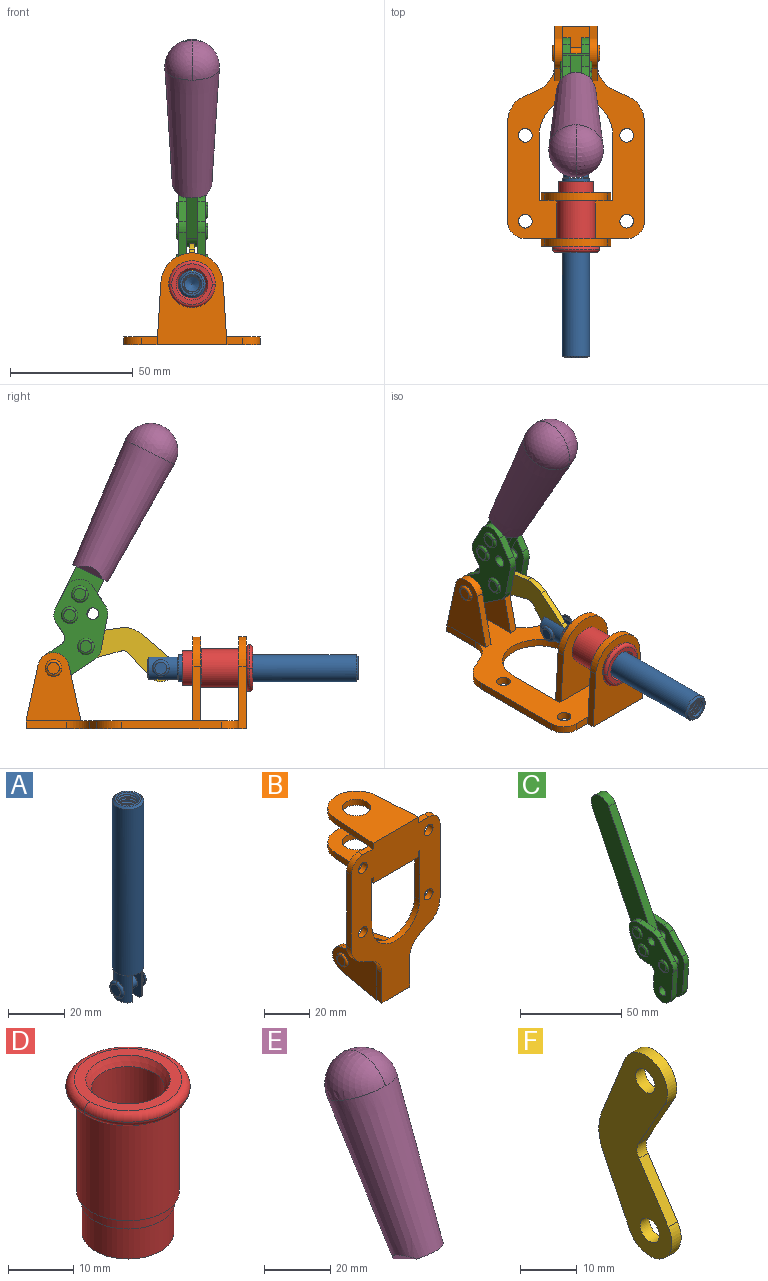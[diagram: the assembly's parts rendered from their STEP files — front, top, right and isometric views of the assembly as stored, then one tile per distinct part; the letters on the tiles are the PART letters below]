
ASSEMBLY  parts=6 mates=6
PART A: 48 faces, bbox 12.6x11.1x86.1 mm
  f0: torus R=2.41mm, axis (-1,0,0), area 15mm2, adj f30,f32,f34
  f1: torus R=2.41mm, axis (-1,0,0), area 15mm2, adj f29,f31,f33
  f2: cylinder r=5.54mm len=72.39mm, axis (0,0,1), area 2518.5mm2, adj f3,f4,f42,f43
  f3: cone r=5.54mm half-angle=45deg, axis (0,0,1), area 7.6mm2, adj f2,f5,f41
  f4: cone r=5.54mm half-angle=45deg, axis (0,0,-1), area 34.9mm2, adj f2,f39
  f5: cylinder r=5.08mm len=11.48mm, axis (0,0,1), area 108.3mm2, adj f3,f7,f8,f41
  f6: cylinder r=2.41mm len=4.83mm, axis (-1,0,0), area 71.2mm2, adj f40,f41
  f7: cylinder r=2.41mm len=4.83mm, axis (-1,0,0), area 7.6mm2, adj f5,f34
  f8: cone r=5.08mm half-angle=45deg, axis (0,0,1), area 10.6mm2, adj f5,f37,f41
  f9: cone r=3.98mm half-angle=45deg, axis (0,0,1), area 17.6mm2, adj f27,f39,f45,f46,f47
  f10: cylinder r=2.41mm len=4.83mm, axis (-1,0,0), area 7.6mm2, adj f33,f38
  f11: cylinder r=3.2mm len=6.4mm, axis (0,0,1), area 78.4mm2, adj f12,f28,f44,f45,f47
  f12: cylinder r=3.2mm len=6.4mm, axis (0,0,1), area 10.5mm2, adj f11,f13,f45,f47
  f13: cylinder r=3.2mm len=6.4mm, axis (0,0,1), area 10.5mm2, adj f12,f14,f45,f47
  f14: cylinder r=3.2mm len=6.4mm, axis (0,0,1), area 10.5mm2, adj f13,f15,f45,f47
  f15: cylinder r=3.2mm len=6.4mm, axis (0,0,1), area 10.5mm2, adj f14,f16,f45,f47
  f16: cylinder r=3.2mm len=6.4mm, axis (0,0,1), area 10.5mm2, adj f15,f17,f45,f47
  f17: cylinder r=3.2mm len=6.4mm, axis (0,0,1), area 10.5mm2, adj f16,f18,f45,f47
  f18: cylinder r=3.2mm len=6.4mm, axis (0,0,1), area 10.5mm2, adj f17,f19,f45,f47
  f19: cylinder r=3.2mm len=6.4mm, axis (0,0,1), area 10.5mm2, adj f18,f20,f45,f47
  f20: cylinder r=3.2mm len=6.4mm, axis (0,0,1), area 10.5mm2, adj f19,f21,f45,f47
  f21: cylinder r=3.2mm len=6.4mm, axis (0,0,1), area 10.5mm2, adj f20,f22,f45,f47
  f22: cylinder r=3.2mm len=6.4mm, axis (0,0,1), area 10.5mm2, adj f21,f23,f45,f47
  f23: cylinder r=3.2mm len=6.4mm, axis (0,0,1), area 10.5mm2, adj f22,f24,f45,f47
  f24: cylinder r=3.2mm len=6.4mm, axis (0,0,1), area 10.5mm2, adj f23,f25,f45,f47
  f25: cylinder r=3.2mm len=6.4mm, axis (0,0,1), area 10.5mm2, adj f24,f26,f45,f47
  f26: cylinder r=3.2mm len=6.4mm, axis (0,0,1), area 10.5mm2, adj f25,f27,f45,f47
  f27: cylinder r=3.2mm len=6.4mm, axis (0,0,1), area 7.4mm2, adj f9,f26,f45,f47
  f28: cone r=3.2mm half-angle=60deg, axis (0,0,1), area 37.2mm2, adj f11
  f29: plane 4.83x4.83mm, normal (-1,0,0), area 18.3mm2, adj f1,f31
  f30: plane 4.83x4.83mm, normal (1,0,0), area 18.3mm2, adj f0,f32
  f31: torus R=2.41mm, axis (-1,0,0), area 15mm2, adj f1,f29,f33
  f32: torus R=2.41mm, axis (-1,0,0), area 15mm2, adj f0,f30,f34
  f33: plane 6.83x6.83mm, normal (1,0,0), area 18.3mm2, adj f1,f10,f31
  f34: plane 6.83x6.83mm, normal (-1,0,0), area 18.3mm2, adj f0,f7,f32
  f35: cone r=5.08mm half-angle=45deg, axis (0,0,1), area 10.6mm2, adj f36,f38,f40
  f36: plane 7.25x1.97mm, normal (0,0,-1), area 10mm2, adj f35,f40
  f37: plane 7.25x1.97mm, normal (0,0,-1), area 10mm2, adj f8,f41
  f38: cylinder r=5.08mm len=11.48mm, axis (0,0,1), area 108.3mm2, adj f10,f35,f40,f42
  f39: plane 9.55x9.55mm, normal (0,0,1), area 22mm2, adj f4,f9
  f40: plane 12.76x10.09mm, normal (1,0,0), area 95.7mm2, adj f6,f35,f36,f38,f42,f43
  f41: plane 12.76x10.09mm, normal (-1,0,0), area 95.7mm2, adj f3,f5,f6,f8,f37,f43
  f42: cone r=5.54mm half-angle=45deg, axis (0,0,1), area 7.6mm2, adj f2,f38,f40
  f43: plane 11.07x4.7mm, normal (0,0,-1), area 50.4mm2, adj f2,f40,f41
  f44: plane 0.89x0.62mm, normal (-1,0,0), area 0.3mm2, adj f11,f45,f46,f47
  f45: bspline ~24.8x7.63mm, area 266.6mm2, adj f9,f11,f12,f13,f14,f15,f16,f17
  f46: bspline ~24.87x7.63mm, area 73.6mm2, adj f9,f44,f45,f47
  f47: bspline ~24.98x7.63mm, area 272.5mm2, adj f9,f11,f12,f13,f14,f15,f16,f17
PART B: 55 faces, bbox 55.7x37.4x89.8 mm
  f0: torus R=2.41mm, axis (-1,0,0), area 15mm2, adj f11,f15,f25
  f1: torus R=2.41mm, axis (-1,0,0), area 15mm2, adj f10,f12,f22
  f2: cylinder r=2.78mm len=5.56mm, axis (0,-1,0), area 54.2mm2, adj f30,f54
  f3: cylinder r=14.99mm len=29.97mm, axis (0,-1,0), area 145.9mm2, adj f30,f49,f53,f54
  f4: cylinder r=2.78mm len=5.56mm, axis (0,-1,0), area 54.2mm2, adj f30,f54
  f5: cylinder r=2.78mm len=5.56mm, axis (0,-1,0), area 54.2mm2, adj f30,f54
  f6: cylinder r=2.78mm len=5.56mm, axis (0,-1,0), area 54.2mm2, adj f30,f54
  f7: cylinder r=6.35mm len=12.7mm, axis (0,0,1), area 123.6mm2, adj f27,f51
  f8: cylinder r=6.35mm len=12.7mm, axis (0,0,-1), area 124.7mm2, adj f21,f35
  f9: cylinder r=2.41mm len=11.18mm, axis (-1,0,0), area 169.4mm2, adj f16,f19
  f10: plane 4.83x4.83mm, normal (1,0,0), area 18.3mm2, adj f1,f12
  f11: plane 4.83x4.83mm, normal (-1,0,0), area 18.3mm2, adj f0,f15
  f12: torus R=2.41mm, axis (-1,0,0), area 15mm2, adj f1,f10,f22
  f13: cylinder r=6.35mm len=12.41mm, axis (1,0,0), area 53.4mm2, adj f18,f19,f22,f23
  f14: cylinder r=6.35mm len=12.41mm, axis (-1,0,0), area 53.4mm2, adj f16,f17,f24,f25
  f15: torus R=2.41mm, axis (-1,0,0), area 15mm2, adj f0,f11,f25
  f16: plane 27.86x22.35mm, normal (1,0,0), area 425.4mm2, adj f9,f14,f17,f24,f30
  f17: plane 22.86x4.97mm, normal (0,0.21,0.98), area 72.5mm2, adj f14,f16,f25,f30
  f18: plane 22.86x4.97mm, normal (0,0.21,0.98), area 72.5mm2, adj f13,f19,f22,f30
  f19: plane 27.86x22.35mm, normal (-1,0,0), area 425.4mm2, adj f9,f13,f18,f23,f30
  f20: cylinder r=12.7mm len=25.35mm, axis (0,0,-1), area 119.8mm2, adj f21,f34,f35,f36
  f21: plane 34.21x28.07mm, normal (0,0,-1), area 702.4mm2, adj f8,f20,f30,f34,f36
  f22: plane 27.96x22.45mm, normal (1,0,0), area 407.2mm2, adj f1,f12,f13,f18,f23,f30,f42,f43
  f23: plane 22.86x4.97mm, normal (0,0.21,-0.98), area 72.5mm2, adj f13,f19,f22,f44
  f24: plane 22.86x4.97mm, normal (0,0.21,-0.98), area 72.5mm2, adj f14,f16,f25,f44
  f25: plane 27.86x22.35mm, normal (-1,0,0), area 407.1mm2, adj f0,f14,f15,f17,f24,f30,f45,f46
  f26: plane 3.1x0.95mm, normal (0,0,-1), area 2.7mm2, adj f30,f49,f50,f54
  f27: plane 34.21x28.07mm, normal (0,0,1), area 702.4mm2, adj f7,f28,f30,f50,f52
  f28: cylinder r=12.7mm len=25.35mm, axis (0,0,1), area 118.8mm2, adj f27,f50,f51,f52
  f29: plane 3.1x0.95mm, normal (0,0,-1), area 2.7mm2, adj f30,f52,f53,f54
  f30: plane 86.54x55.63mm, normal (0,1,0), area 2362.9mm2, adj f2,f3,f4,f5,f6,f16,f17,f18
  f31: plane 40.56x3.1mm, normal (-1,0,0), area 125.7mm2, adj f30,f32,f48,f54
  f32: cylinder r=7.11mm len=7.11mm, axis (0,-1,0), area 34.6mm2, adj f30,f31,f33,f54
  f33: plane 6.67x3.1mm, normal (0,0,1), area 20.4mm2, adj f30,f32,f34,f54
  f34: plane 25.39x3.13mm, normal (-1,0.06,0), area 79.5mm2, adj f20,f21,f33,f35,f54
  f35: plane 37.31x28.45mm, normal (0,0,1), area 789.9mm2, adj f8,f20,f34,f36,f54
  f36: plane 25.39x3.13mm, normal (1,0.06,0), area 79.5mm2, adj f20,f21,f35,f37,f54
  f37: plane 6.67x3.1mm, normal (0,0,1), area 20.4mm2, adj f30,f36,f38,f54
  f38: cylinder r=7.11mm len=7.11mm, axis (0,-1,0), area 34.6mm2, adj f30,f37,f39,f54
  f39: plane 40.56x3.1mm, normal (1,0,0), area 125.7mm2, adj f30,f38,f40,f54
  f40: cylinder r=11.18mm len=10.16mm, axis (0,-1,0), area 39.5mm2, adj f30,f39,f41,f54
  f41: plane 6.09x3.1mm, normal (0.42,0,-0.91), area 20.8mm2, adj f30,f40,f42,f54
  f42: cylinder r=11.18mm len=9.41mm, axis (0,-1,0), area 37.2mm2, adj f22,f30,f41,f43,f54
  f43: plane 16.5x3.1mm, normal (1,0,0), area 51.1mm2, adj f22,f42,f44,f54
  f44: plane 17.37x3.1mm, normal (0,0,-1), area 53.8mm2, adj f23,f24,f30,f43,f45,f54
  f45: plane 16.5x3.1mm, normal (-1,0,0), area 51.1mm2, adj f25,f44,f46,f54
  f46: cylinder r=11.18mm len=9.41mm, axis (0,-1,0), area 37.2mm2, adj f25,f30,f45,f47,f54
  f47: plane 6.09x3.1mm, normal (-0.42,0,-0.91), area 20.8mm2, adj f30,f46,f48,f54
  f48: cylinder r=11.18mm len=10.16mm, axis (0,-1,0), area 39.5mm2, adj f30,f31,f47,f54
  f49: plane 26.54x3.1mm, normal (-1,0,0), area 82.3mm2, adj f3,f26,f30,f54
  f50: plane 25.39x3.1mm, normal (1,0.06,0), area 78.8mm2, adj f26,f27,f28,f51,f54
  f51: plane 37.31x28.45mm, normal (0,0,-1), area 789.9mm2, adj f7,f28,f50,f52,f54
  f52: plane 25.39x3.1mm, normal (-1,0.06,0), area 78.8mm2, adj f27,f28,f29,f51,f54
  f53: plane 26.54x3.1mm, normal (1,0,0), area 82.3mm2, adj f3,f29,f30,f54
  f54: plane 89.66x55.63mm, normal (0,-1,0), area 2678.5mm2, adj f2,f3,f4,f5,f6,f26,f29,f31
PART C: 59 faces, bbox 12.9x60.2x99.6 mm
  f0: torus R=2.39mm, axis (-1,0,0), area 14.9mm2, adj f20,f43,f51
  f1: torus R=2.39mm, axis (-1,0,0), area 14.9mm2, adj f19,f42,f51
  f2: torus R=2.39mm, axis (-1,0,0), area 14.9mm2, adj f18,f35,f51
  f3: torus R=2.39mm, axis (-1,0,0), area 14.9mm2, adj f14,f17,f23
  f4: torus R=2.39mm, axis (-1,0,0), area 14.9mm2, adj f13,f16,f23
  f5: torus R=2.39mm, axis (-1,0,0), area 14.9mm2, adj f12,f15,f23
  f6: cylinder r=2.39mm len=4.78mm, axis (1,0,0), area 46.5mm2, adj f48,f50,f51
  f7: cylinder r=2.39mm len=4.78mm, axis (1,0,0), area 46.5mm2, adj f50,f51
  f8: cylinder r=6.35mm len=12.68mm, axis (1,0,0), area 61.8mm2, adj f38,f39,f50,f51
  f9: cylinder r=2.39mm len=4.78mm, axis (-1,0,0), area 70.5mm2, adj f46,f50
  f10: cylinder r=2.39mm len=4.78mm, axis (-1,0,0), area 46.5mm2, adj f23,f45,f46
  f11: cylinder r=2.39mm len=4.78mm, axis (-1,0,0), area 46.5mm2, adj f23,f46
  f12: plane 4.78x4.78mm, normal (1,0,0), area 17.9mm2, adj f5,f15
  f13: plane 4.78x4.78mm, normal (1,0,0), area 17.9mm2, adj f4,f16
  f14: plane 4.78x4.78mm, normal (1,0,0), area 17.9mm2, adj f3,f17
  f15: torus R=2.39mm, axis (-1,0,0), area 14.9mm2, adj f5,f12,f23
  f16: torus R=2.39mm, axis (-1,0,0), area 14.9mm2, adj f4,f13,f23
  f17: torus R=2.39mm, axis (-1,0,0), area 14.9mm2, adj f3,f14,f23
  f18: plane 4.78x4.78mm, normal (-1,0,0), area 17.9mm2, adj f2,f35
  f19: plane 4.78x4.78mm, normal (-1,0,0), area 17.9mm2, adj f1,f42
  f20: plane 4.78x4.78mm, normal (-1,0,0), area 17.9mm2, adj f0,f43
  f21: plane 2.26x0.2mm, normal (1,0,0), area 0.2mm2, adj f31,f44
  f22: plane 2.26x0.2mm, normal (-1,0,0), area 0.2mm2, adj f41,f44
  f23: plane 39.37x30.77mm, normal (1,0,0), area 565.5mm2, adj f3,f4,f5,f10,f11,f15,f16,f17
  f24: cylinder r=6.1mm len=4.15mm, axis (-1,0,0), area 14.7mm2, adj f23,f25,f32,f46
  f25: plane 10.25x9.01mm, normal (0,-0.75,0.66), area 42.3mm2, adj f23,f24,f26,f46
  f26: cylinder r=6.35mm len=4.64mm, axis (-1,0,0), area 15.6mm2, adj f23,f25,f27,f46
  f27: plane 15.84x3.1mm, normal (0,-1,-0.07), area 49.2mm2, adj f23,f26,f28,f46
  f28: cylinder r=6.35mm len=12.68mm, axis (-1,0,0), area 61.8mm2, adj f23,f27,f29,f46
  f29: plane 8.11x3.1mm, normal (0,1,0.07), area 25.2mm2, adj f23,f28,f30,f46
  f30: cylinder r=3.05mm len=3.25mm, axis (-1,0,0), area 14.8mm2, adj f23,f29,f31,f46
  f31: plane 5.99x3.1mm, normal (0,0.07,-1), area 18.6mm2, adj f21,f23,f30,f44,f46
  f32: plane 9.5x3.1mm, normal (0,-0.07,1), area 29.5mm2, adj f23,f24,f33,f46,f47
  f33: cylinder r=6.1mm len=8.63mm, axis (-1,0,0), area 39.1mm2, adj f23,f32,f34,f47
  f34: plane 8.65x3.96mm, normal (0,0.91,-0.42), area 29.5mm2, adj f23,f33,f44,f47
  f35: torus R=2.39mm, axis (-1,0,0), area 14.9mm2, adj f2,f18,f51
  f36: plane 10.25x9.01mm, normal (0,-0.75,0.66), area 42.3mm2, adj f37,f49,f50,f51
  f37: cylinder r=6.35mm len=4.64mm, axis (1,0,0), area 15.6mm2, adj f36,f38,f50,f51
  f38: plane 15.84x3.1mm, normal (0,-1,-0.07), area 49.2mm2, adj f8,f37,f50,f51
  f39: plane 8.11x3.1mm, normal (0,1,0.07), area 25.2mm2, adj f8,f40,f50,f51
  f40: cylinder r=3.05mm len=3.25mm, axis (1,0,0), area 14.8mm2, adj f39,f41,f50,f51
  f41: plane 5.99x3.1mm, normal (0,0.07,-1), area 18.6mm2, adj f22,f40,f44,f50,f51
  f42: torus R=2.39mm, axis (-1,0,0), area 14.9mm2, adj f1,f19,f51
  f43: torus R=2.39mm, axis (-1,0,0), area 14.9mm2, adj f0,f20,f51
  f44: cylinder r=6.35mm len=12.12mm, axis (-1,0,0), area 128.9mm2, adj f21,f22,f23,f31,f34,f41,f46,f47
  f45: plane 2.65x1.35mm, normal (1,0,0), area 1mm2, adj f10,f55
  f46: plane 39.08x20.42mm, normal (-1,0,0), area 412.5mm2, adj f9,f10,f11,f24,f25,f26,f27,f28
  f47: plane 77.62x39.82mm, normal (1,0,0), area 850mm2, adj f32,f33,f34,f44,f53,f54,f55
  f48: plane 2.65x1.35mm, normal (-1,0,0), area 1mm2, adj f6,f55
  f49: cylinder r=6.1mm len=4.15mm, axis (1,0,0), area 14.7mm2, adj f36,f50,f51,f56
  f50: plane 39.08x20.42mm, normal (1,0,0), area 412.5mm2, adj f6,f7,f8,f9,f36,f37,f38,f39
  f51: plane 39.37x30.77mm, normal (-1,0,0), area 565.5mm2, adj f0,f1,f2,f6,f7,f8,f35,f36
  f52: plane 8.65x3.96mm, normal (0,0.91,-0.42), area 29.5mm2, adj f44,f51,f57,f58
  f53: plane 68.49x33.4mm, normal (0,0.9,-0.44), area 358.1mm2, adj f44,f47,f54,f58
  f54: cylinder r=6.35mm len=12.06mm, axis (1,0,0), area 93.7mm2, adj f47,f53,f55,f58
  f55: plane 68.49x33.4mm, normal (0,-0.9,0.44), area 358.1mm2, adj f44,f45,f46,f47,f48,f50,f54,f58
  f56: plane 9.5x3.1mm, normal (0,-0.07,1), area 29.5mm2, adj f49,f50,f51,f57,f58
  f57: cylinder r=6.1mm len=8.63mm, axis (1,0,0), area 39.1mm2, adj f51,f52,f56,f58
  f58: plane 77.62x39.82mm, normal (-1,0,0), area 850mm2, adj f44,f52,f53,f54,f55,f56,f57
PART D: 15 faces, bbox 20.6x20.6x28.7 mm
  f0: torus R=8.26mm, axis (0,0,1), area 56.8mm2, adj f1,f10,f12
  f1: torus R=8.26mm, axis (0,0,1), area 56.8mm2, adj f0,f6,f13
  f2: cylinder r=5.59mm len=25.91mm, axis (0,0,1), area 909.6mm2, adj f3,f4
  f3: cone r=6.86mm half-angle=45deg, axis (0,0,-1), area 70.2mm2, adj f2,f14
  f4: cone r=6.47mm half-angle=30deg, axis (0,0,1), area 66.7mm2, adj f2,f13
  f5: cylinder r=7.04mm len=14.07mm, axis (0,0,1), area 252.6mm2, adj f11,f14
  f6: torus R=8.26mm, axis (0,0,1), area 56.8mm2, adj f1,f12,f13
  f7: cylinder r=7.16mm len=14.33mm, axis (0,0,1), area 91.5mm2, adj f9,f11
  f8: cylinder r=7.86mm len=18.42mm, axis (0,0,1), area 909.6mm2, adj f9,f10
  f9: plane 15.72x15.72mm, normal (0,0,-1), area 33mm2, adj f7,f8
  f10: plane 16.51x16.51mm, normal (0,0,-1), area 19.9mm2, adj f0,f8,f12
  f11: plane 14.33x14.33mm, normal (0,0,-1), area 5.7mm2, adj f5,f7
  f12: torus R=8.26mm, axis (0,0,1), area 56.8mm2, adj f0,f6,f10
  f13: plane 16.51x16.51mm, normal (0,0,1), area 82.7mm2, adj f1,f4,f6
  f14: plane 14.07x14.07mm, normal (0,0,-1), area 7.8mm2, adj f3,f5
PART E: 11 faces, bbox 22.3x42.6x64.5 mm
  f0: sphere r=11.13mm, area 411.4mm2, adj f1,f8
  f1: cone r=11.11mm half-angle=3.3deg, axis (0,0.44,0.9), area 3251.8mm2, adj f0,f7,f8,f9,f10
  f2: cylinder r=6.16mm len=11.7mm, axis (1,0,0), area 89.5mm2, adj f3,f4,f5,f6
  f3: plane 60.23x36.75mm, normal (-1,0,0), area 763.6mm2, adj f2,f4,f6,f10
  f4: plane 51.37x25.05mm, normal (0,0.9,-0.44), area 264.2mm2, adj f2,f3,f5,f10
  f5: plane 60.23x36.75mm, normal (1,0,0), area 763.6mm2, adj f2,f4,f6,f10
  f6: plane 51.37x25.05mm, normal (0,-0.9,0.44), area 264.2mm2, adj f2,f3,f5,f10
  f7: plane 9.95x5.95mm, normal (0.71,-0.31,-0.64), area 25.8mm2, adj f1,f10
  f8: sphere r=11.13mm, area 411.4mm2, adj f0,f1
  f9: plane 9.95x5.95mm, normal (-0.71,-0.31,-0.64), area 25.8mm2, adj f1,f10
  f10: plane 14.27x11.38mm, normal (0,-0.44,-0.9), area 106.7mm2, adj f1,f3,f4,f5,f6,f7,f9
PART F: 12 faces, bbox 2.3x18.2x42.8 mm
  f0: cylinder r=2.4mm len=4.8mm, axis (1,0,0), area 34.9mm2, adj f4,f11
  f1: cylinder r=10.41mm len=8.47mm, axis (1,0,0), area 20.2mm2, adj f4,f9,f10,f11
  f2: cylinder r=3.05mm len=3.16mm, axis (1,0,0), area 7.7mm2, adj f4,f6,f7,f11
  f3: cylinder r=2.4mm len=4.8mm, axis (1,0,0), area 34.9mm2, adj f4,f11
  f4: plane 42.81x18.23mm, normal (-1,0,0), area 414.1mm2, adj f0,f1,f2,f3,f5,f6,f7,f8
  f5: cylinder r=5.54mm len=10.67mm, axis (1,0,0), area 41.8mm2, adj f4,f6,f10,f11
  f6: plane 11.66x6.53mm, normal (0,-0.87,-0.49), area 30.9mm2, adj f2,f4,f5,f11
  f7: plane 11.17x7.33mm, normal (0,-0.84,0.55), area 30.9mm2, adj f2,f4,f8,f11
  f8: cylinder r=5.54mm len=10.51mm, axis (1,0,0), area 41.8mm2, adj f4,f7,f9,f11
  f9: plane 13.67x6.67mm, normal (0,0.9,-0.44), area 35.1mm2, adj f1,f4,f8,f11
  f10: plane 14.1x5.7mm, normal (0,0.93,0.37), area 35.1mm2, adj f1,f4,f5,f11
  f11: plane 42.81x18.23mm, normal (1,0,0), area 414.1mm2, adj f0,f1,f2,f3,f5,f6,f7,f8
PLACE A rot(axis=(1,0,0),90deg) t=(0,13.02,0)mm
PLACE B rot(axis=(1,0,0),90deg) t=(0,9.14,0)mm fixed
PLACE C rot(axis=(1,0,0),52.2deg) t=(0,0.79,24.84)mm
PLACE D rot(axis=(1,0,0),90deg) t=(0,9.14,0)mm
PLACE E rot(axis=(1,0,0),52.2deg) t=(0.04,0.79,24.84)mm
PLACE F rot(axis=(1,0,0),108.2deg) t=(0,19.92,6.05)mm
MATE revolute F.f3 <-> C.f4  axis (1,0,0) through (0,28.04,33.45)mm
MATE fastened E.f2 <-> C.f54  axis (-1,0,0) through (2.35,1.06,114.54)mm
MATE revolute C.f7 <-> B.f0  axis (-1,0,0) through (0,41.23,24.61)mm
MATE slider A.f2 <-> B.f7  axis (0,-1,0) through (0,-45.76,24.61)mm
MATE fastened D.f2 <-> B.f7  axis (0,1,0) through (0,-37.25,24.61)mm
MATE revolute F.f5 <-> A.f6  axis (1,0,0) through (0,-2.45,24.61)mm
